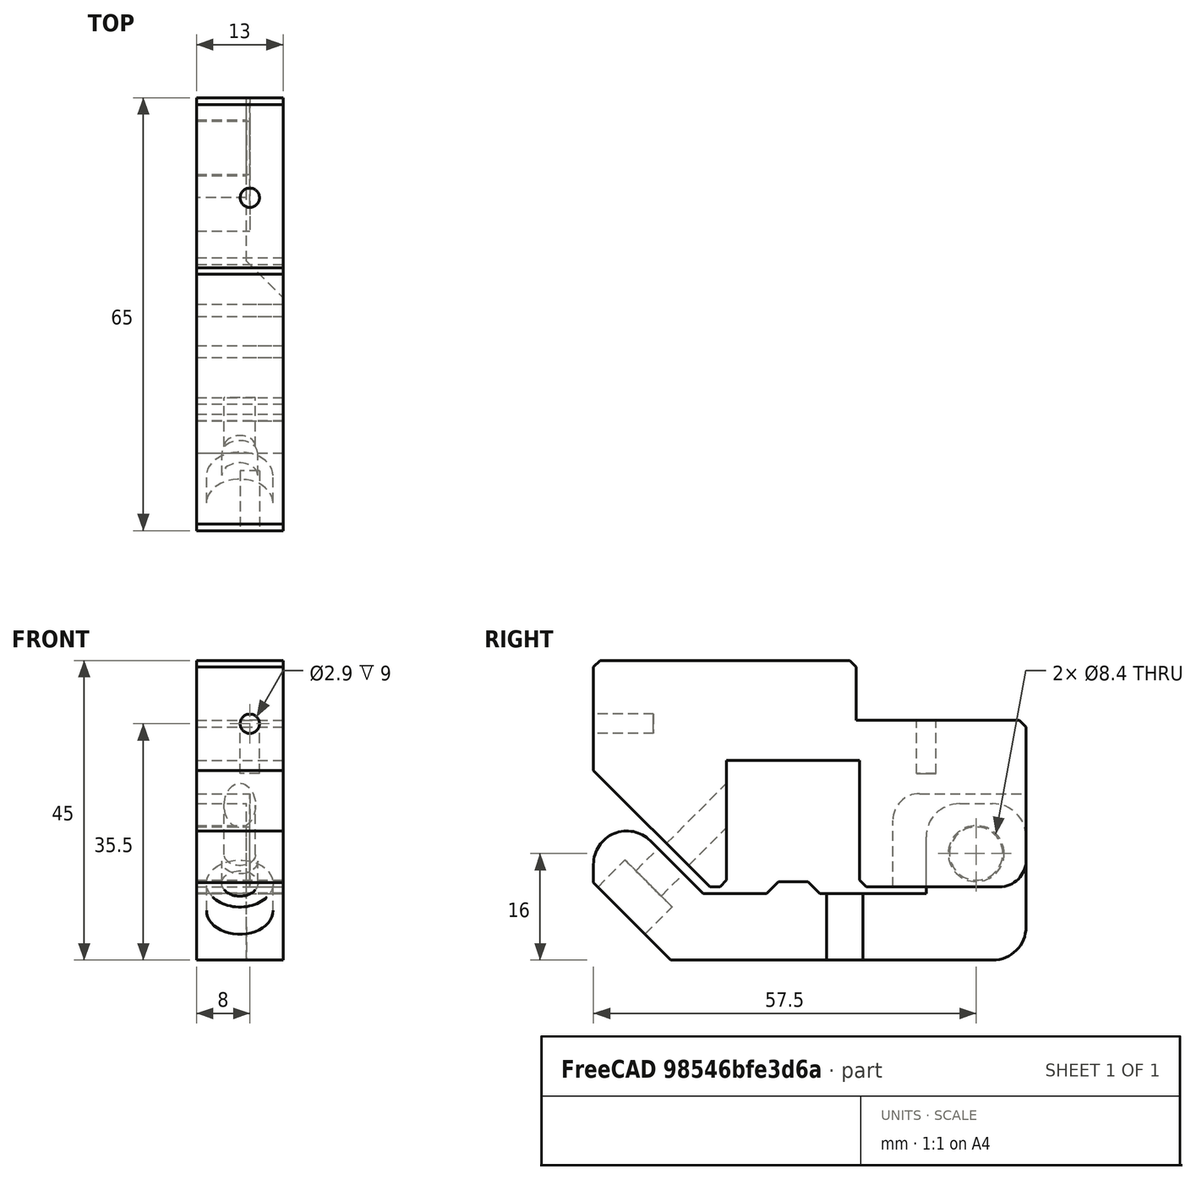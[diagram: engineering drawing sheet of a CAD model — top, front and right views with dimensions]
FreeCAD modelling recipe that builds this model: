
FCSTD DOCUMENT  (FreeCAD 0.18.4R)
Label: 0816_adaptor_8mm
License: All rights reserved
LicenseURL: http://en.wikipedia.org/wiki/All_rights_reserved
objects: Part::Box×14, Part::Cut×10, Part::Cylinder×7, Part::MultiFuse×6, PartDesign::Chamfer×3, PartDesign::FeatureBase×2, PartDesign::Fillet×2, PartDesign::Body×2, Part::Feature×2
note: 48 computed .brp shape members not serialized (recipe doc carries the construction recipe); baked Part::Feature solids carry a one-line shape summary decoded from their .brp

FEATURE [Part::Box] Box  label="Cube"
  AttacherType = Attacher::AttachEngine3D
  Height = 20
  Length = 13
  Width = 20
FEATURE [Part::Box] Box001  label="Cube_base"
  AttacherType = Attacher::AttachEngine3D
  Height = 35
  Length = 13
  Placement = pos=(0,-20,0) rot=(0,0,1;0rad)
  Width = 65
FEATURE [Part::Box] Box002  label="Cube002"
  AttacherType = Attacher::AttachEngine3D
  Height = 9
  Length = 13
  Placement = pos=(0,19.5,26) rot=(0,0,1;0rad)
  Width = 25.5
FEATURE [Part::Cylinder] Cylinder
  Angle = 360
  AttacherType = Attacher::AttachEngine3D
  Height = 10
  Placement = pos=(8,30,18) rot=(0,0,1;0rad)
  Radius = 1.45
FEATURE [Part::Cylinder] Cylinder001
  Angle = 360
  AttacherType = Attacher::AttachEngine3D
  Height = 15
  Placement = pos=(6.5,-8.89949,4.34315) rot=(-1,0,0;0.785398rad)
  Radius = 2.35
FEATURE [Part::Cylinder] Cylinder002
  Angle = 360
  AttacherType = Attacher::AttachEngine3D
  Height = 10
  Placement = pos=(8,-11,25.5) rot=(1,0,0;1.5708rad)
  Radius = 1.45
FEATURE [Part::Box] Box003  label="cube_45deg"
  AttacherType = Attacher::AttachEngine3D
  Height = 50
  Length = 13
  Placement = pos=(0,-18.4853,-18.3848) rot=(1,0,0;0.785398rad)
  Width = 25
FEATURE [Part::MultiFuse] Fusion
  Shapes = -> [Box,Box002,Box003]
FEATURE [Part::Cut] Cut
  Base = -> Box001
  Tool = -> Fusion
FEATURE [Part::Box] Box004  label="Cube003"
  AttacherType = Attacher::AttachEngine3D
  Height = 15
  Length = 8
  Placement = pos=(0,25,0) rot=(0,0,1;0rad)
  Width = 20
FEATURE [Part::Cut] Cut001
  Base = -> Cut
  Tool = -> Box004
FEATURE [Part::Cylinder] Cylinder004
  Angle = 360
  AttacherType = Attacher::AttachEngine3D
  Height = 10
  Placement = pos=(-1.1e-15,37.5,6) rot=(0,1,0;1.5708rad)
  Radius = 4
FEATURE [Part::Box] Box005  label="Cube004"
  AttacherType = Attacher::AttachEngine3D
  Height = 10
  Length = 7.5
  Placement = pos=(0,-20,-10) rot=(0,0,1;0rad)
  Width = 65
FEATURE [Part::Box] Box006  label="Cube005+"
  AttacherType = Attacher::AttachEngine3D
  Height = 14
  Length = 7.5
  Placement = pos=(0,30,-0.5) rot=(0,0,1;0rad)
  Width = 15
FEATURE [Part::MultiFuse] Fusion001  label="fusion holes"
  Shapes = -> [Cylinder,Cylinder002,Cylinder001]
FEATURE [Part::Cut] Cut002
  Base = -> Cut001
  Tool = -> Fusion001
FEATURE [Part::MultiFuse] Fusion002
  Shapes = -> [Cut002,Cylinder004]
FEATURE [Part::Cylinder] Cylinder005  label="Cylinder005-"
  Angle = 360
  AttacherType = Attacher::AttachEngine3D
  Height = 10
  Placement = pos=(-1.1e-15,37.5,6) rot=(0,1,0;1.5708rad)
  Radius = 4.2
FEATURE [Part::MultiFuse] Fusion003
  Shapes = -> [Box005,Box006]
FEATURE [Part::Cut] Cut003
  Base = -> Fusion003
  Tool = -> Cylinder005
FEATURE [Part::Box] Box007  label="Cube006"
  AttacherType = Attacher::AttachEngine3D
  Height = 30
  Length = 13
  Placement = pos=(0,-20,-0.5) rot=(0,0,1;0rad)
  Width = 20
FEATURE [Part::Box] Box008  label="Cube007"
  AttacherType = Attacher::AttachEngine3D
  Height = 50
  Length = 13
  Placement = pos=(0,-3.53553,0) rot=(1,0,0;0.785398rad)
  Width = 30
FEATURE [Part::Cut] Cut004
  Base = -> Box007
  Tool = -> Box008
FEATURE [Part::Box] Box009  label="Cube008-"
  AttacherType = Attacher::AttachEngine3D
  Height = 10
  Length = 13
  Placement = pos=(0,-3.5,-0.5) rot=(0,0,1;0rad)
  Width = 10
FEATURE [Part::Cut] Cut005
  Base = -> Cut004
  Tool = -> Box009
FEATURE [Part::Cylinder] Cylinder006  label="Cylinder006-"
  Angle = 360
  AttacherType = Attacher::AttachEngine3D
  Height = 20
  Placement = pos=(6.5,-22.3345,-9.09188) rot=(-1,0,0;0.785398rad)
  Radius = 2.7
FEATURE [Part::Box] Box010  label="Cube009+"
  AttacherType = Attacher::AttachEngine3D
  Height = 10
  Length = 5.5
  Placement = pos=(7.5,-20,-10) rot=(0,0,1;0rad)
  Width = 35
FEATURE [Part::MultiFuse] Fusion004
  Shapes = -> [Box010,Cut005,Cut003]
FEATURE [Part::Cut] Cut006
  Base = -> Fusion004
  Tool = -> Cylinder006
FEATURE [Part::Box] Box011  label="Cube008-001"
  AttacherType = Attacher::AttachEngine3D
  Height = 50
  Length = 13
  Placement = pos=(0,-24.0416,-36.7696) rot=(1,0,0;0.785398rad)
  Width = 30
FEATURE [Part::Cut] Cut007
  Base = -> Cut006
  Tool = -> Box011
FEATURE [Part::Box] Box012  label="Cube008"
  AttacherType = Attacher::AttachEngine3D
  Height = 1
  Length = 13
  Placement = pos=(0,-20,0) rot=(0,0,1;0rad)
  Width = 65
FEATURE [Part::Cut] Cut008  label="Top_part"
  Base = -> Fusion002
  Tool = -> Box012
FEATURE [Part::Cylinder] Cylinder007  label="Cylinder006-001"
  Angle = 360
  AttacherType = Attacher::AttachEngine3D
  Height = 6
  Placement = pos=(6.5,-15.9706,-2.72792) rot=(-1,0,0;0.785398rad)
  Radius = 5
FEATURE [Part::Cut] Cut009  label="cutXXX"
  Base = -> Cut007
  Tool = -> Cylinder007
FEATURE [Part::Box] Box013  label="Cube009"
  AttacherType = Attacher::AttachEngine3D
  Height = 1.8
  Length = 13
  Placement = pos=(0,7.8,0) rot=(0,0,1;0rad)
  Width = 4.4
FEATURE [Part::MultiFuse] Fusion005  label="Bottom_part"
  Shapes = -> [Cut009,Box013]
FEATURE [PartDesign::FeatureBase] BaseFeature
  BaseFeature = -> Cut008
FEATURE [PartDesign::Chamfer] Chamfer
  Base = -> BaseFeature [Edge14,Edge44,Edge42,Edge46,Edge19]
  BaseFeature = -> BaseFeature
  Size = 1
FEATURE [PartDesign::Fillet] Fillet
  Base = -> Chamfer [Edge3,Edge46]
  BaseFeature = -> Chamfer
  Radius = 4
FEATURE [PartDesign::Body] Body
  BaseFeature = -> Cut008
  Group = -> [BaseFeature,Chamfer,Fillet]
  Origin = -> Origin
  Tip = -> Fillet
FEATURE [Part::Feature] Fillet003  label="refined_top"
  shape: bbox 13 x 65 x 34 mm, 30 faces (baked)
FEATURE [PartDesign::FeatureBase] BaseFeature001
  BaseFeature = -> Fusion005
FEATURE [PartDesign::Fillet] Fillet004
  Base = -> BaseFeature001 [Edge87,Edge59,Edge77,Edge40]
  BaseFeature = -> BaseFeature001
  Radius = 5
FEATURE [PartDesign::Chamfer] Chamfer001
  Base = -> Fillet004 [Edge44]
  BaseFeature = -> Fillet004
  Size = 5.49
FEATURE [PartDesign::Chamfer] Chamfer002
  Base = -> Chamfer001 [Edge72,Edge40,Edge58,Edge84]
  BaseFeature = -> Chamfer001
  Size = 1.79
FEATURE [PartDesign::Body] Body001
  BaseFeature = -> Fusion005
  Group = -> [BaseFeature001,Fillet004,Chamfer001,Chamfer002]
  Origin = -> Origin001
  Tip = -> Chamfer002
FEATURE [Part::Feature] Chamfer002001  label="refined_bottom"
  shape: bbox 13 x 65 x 23.5 mm, 29 faces (baked)
